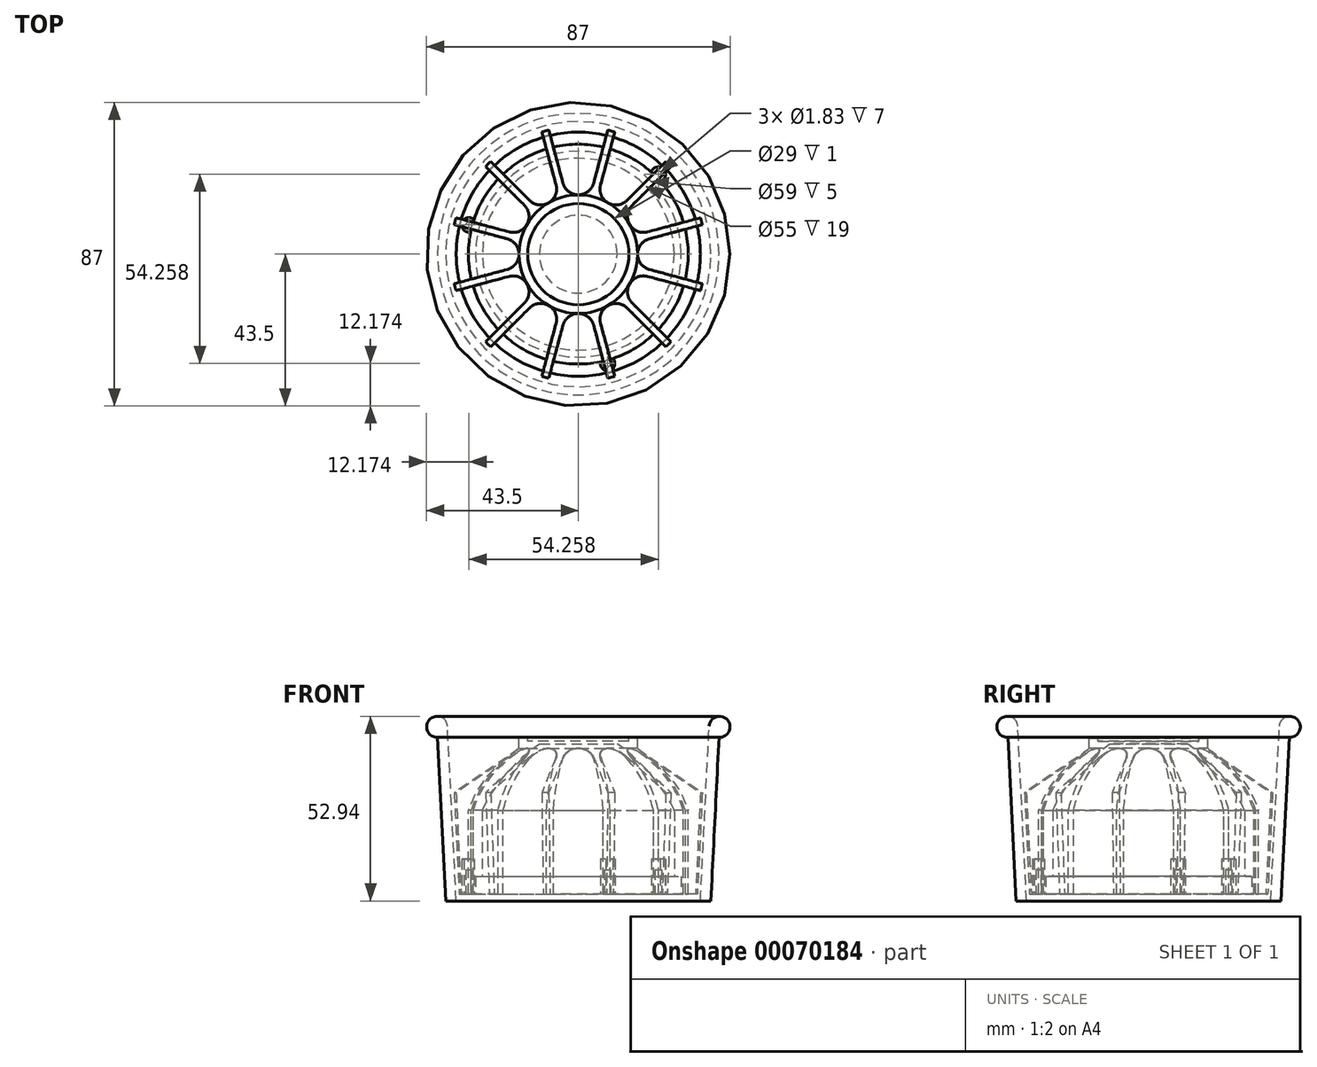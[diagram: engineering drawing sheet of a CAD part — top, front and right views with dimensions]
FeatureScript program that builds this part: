
annotation { "Feature Type Name" : "Feature", "Feature Type Description" : "" }
export const myFeature = defineFeature(function(context is Context, id is Id, definition is map)
    precondition{}
    {
        {
            var Q0;
            Q0=qCreatedBy(makeId("Right.planeOp"),FACE);
            var sketch = newSketch(context, id + "F0", { "sketchPlane" : qUnion([Q0])});
            skLineSegment(sketch, "E0.bottom", {"start": v(37.5, 50.09) * mm, "end": v(40.5, 49.94) * mm});
            skLineSegment(sketch, "E0.top", {"start": v(35, 0) * mm, "end": v(38, 0) * mm});
            skLineSegment(sketch, "E0.left", {"start": v(37.5, 50.09) * mm, "end": v(36.55, 31.11) * mm});
            skLineSegment(sketch, "E0.right", {"start": v(40.5, 49.94) * mm, "end": v(38, 0) * mm});
            skLineSegment(sketch, "E1", {"start": v(36.55, 31.11) * mm, "end": v(17, 43.74) * mm});
            skLineSegment(sketch, "E2", {"start": v(17, 43.74) * mm, "end": v(17, 46.74) * mm});
            skLineSegment(sketch, "E3", {"start": v(17, 46.74) * mm, "end": v(14.5, 46.74) * mm});
            skLineSegment(sketch, "E4", {"start": v(14.5, 46.74) * mm, "end": v(14.5, 45.74) * mm});
            skLineSegment(sketch, "E5", {"start": v(14.5, 45.74) * mm, "end": v(0, 45.74) * mm});
            skLineSegment(sketch, "E6", {"start": v(0, 45.74) * mm, "end": v(0, 0) * mm});
            skLineSegment(sketch, "E7", {"start": v(0, 0) * mm, "end": v(35, 0) * mm});
            skPoint(sketch, "E8.second.point", {"position": v(33.82, 50.09) * mm});
            skArc(sketch, "E9", {"start": v(40.35, 46.94) * mm, "mid": v(42.72, 51.95) * mm, "end": v(37.5, 50.09) * mm});
            skSolve(sketch);
        }
        {
            var Q0;
            {var subQ0=sQuery(id+"F0.wireOp",EDGE,"E0.top");Q0=makeQuery(id+"F0.imprint","IMPRINT",FACE,{"disambiguationData":[TD([[makeQuery(id+"F0.imprint","IMPRINT",EDGE,{"derivedFrom":subQ0}),1.0]])]});}
            var Q1;
            {var subQ0=sQuery(id+"F0.wireOp",EDGE,"E0.bottom");Q1=makeQuery(id+"F0.imprint","IMPRINT",FACE,{"disambiguationData":[TD([[makeQuery(id+"F0.imprint","IMPRINT",EDGE,{"derivedFrom":subQ0}),-1.0]])]});}
            var Q2;
            {var subQ0=sQuery(id+"F0.wireOp",EDGE,"E0.bottom");Q2=makeQuery(id+"F0.imprint","IMPRINT",FACE,{"disambiguationData":[TD([[makeQuery(id+"F0.imprint","IMPRINT",EDGE,{"derivedFrom":subQ0}),1.0]])]});}
            var Q3;
            Q3=sQuery(id+"F0.wireOp",EDGE,"E6");
            revolve(context, id + "F1", {"entities" : qUnion([Q0, Q1, Q2]), "axis" : qUnion([Q3]), "revolveType" : RevolveType.FULL});
        }
        {
            var Q0;
            Q0=makeQuery(id+"F1.opRevolve","SWEPT_FACE",FACE,{"disambiguationData":[OSD([sQuery(id+"F0.wireOp",EDGE,"E5")])]});
            var sketch = newSketch(context, id + "F2", { "sketchPlane" : qUnion([Q0])});
            skCircle(sketch, "E10.0", {"center": v(0, 0) * mm, "radius": 37.5 * mm, "construction": true});
            skCircle(sketch, "E11.0", {"center": v(0, 0) * mm, "radius": 17 * mm, "construction": true});
            skLineSegment(sketch, "E12", {"start": v(-8.71, 36.47) * mm, "end": v(-4.4, 20.37) * mm});
            skLineSegment(sketch, "E13", {"start": v(8.71, 36.47) * mm, "end": v(4.4, 20.37) * mm});
            skArc(sketch, "E14", {"start": v(-4.4, 20.37) * mm, "mid": v(-2.77, 17.94) * mm, "end": v(0, 17) * mm});
            skArc(sketch, "E15", {"start": v(0, 17) * mm, "mid": v(2.77, 17.94) * mm, "end": v(4.4, 20.37) * mm});
            skArc(sketch, "E16", {"start": v(8.71, 36.47) * mm, "mid": v(0, 37.5) * mm, "end": v(-8.71, 36.47) * mm});
            skLineSegment(sketch, "E17.1.0", {"start": v(25.78, 27.23) * mm, "end": v(14, 15.45) * mm});
            skArc(sketch, "E17.1.1", {"start": v(8.5, 14.72) * mm, "mid": v(11.37, 14.15) * mm, "end": v(14, 15.45) * mm});
            skArc(sketch, "E17.1.2", {"start": v(6.38, 19.84) * mm, "mid": v(6.57, 16.92) * mm, "end": v(8.5, 14.72) * mm});
            skLineSegment(sketch, "E17.1.3", {"start": v(10.7, 35.94) * mm, "end": v(6.38, 19.84) * mm});
            skArc(sketch, "E17.1.4", {"start": v(25.78, 27.23) * mm, "mid": v(18.75, 32.48) * mm, "end": v(10.7, 35.94) * mm});
            skLineSegment(sketch, "E17.2.0", {"start": v(35.94, 10.7) * mm, "end": v(19.84, 6.38) * mm});
            skArc(sketch, "E17.2.1", {"start": v(14.72, 8.5) * mm, "mid": v(16.92, 6.57) * mm, "end": v(19.84, 6.38) * mm});
            skArc(sketch, "E17.2.2", {"start": v(15.45, 14) * mm, "mid": v(14.15, 11.37) * mm, "end": v(14.72, 8.5) * mm});
            skLineSegment(sketch, "E17.2.3", {"start": v(27.23, 25.78) * mm, "end": v(15.45, 14) * mm});
            skArc(sketch, "E17.2.4", {"start": v(35.94, 10.7) * mm, "mid": v(32.48, 18.75) * mm, "end": v(27.23, 25.78) * mm});
            skLineSegment(sketch, "E17.3.0", {"start": v(36.47, -8.71) * mm, "end": v(20.37, -4.4) * mm});
            skArc(sketch, "E17.3.1", {"start": v(17, 0) * mm, "mid": v(17.94, -2.77) * mm, "end": v(20.37, -4.4) * mm});
            skArc(sketch, "E17.3.2", {"start": v(20.37, 4.4) * mm, "mid": v(17.94, 2.77) * mm, "end": v(17, 0) * mm});
            skLineSegment(sketch, "E17.3.3", {"start": v(36.47, 8.71) * mm, "end": v(20.37, 4.4) * mm});
            skArc(sketch, "E17.3.4", {"start": v(36.47, -8.71) * mm, "mid": v(37.5, 0) * mm, "end": v(36.47, 8.71) * mm});
            skLineSegment(sketch, "E17.4.0", {"start": v(27.23, -25.78) * mm, "end": v(15.45, -14) * mm});
            skArc(sketch, "E17.4.1", {"start": v(14.72, -8.5) * mm, "mid": v(14.15, -11.37) * mm, "end": v(15.45, -14) * mm});
            skArc(sketch, "E17.4.2", {"start": v(19.84, -6.38) * mm, "mid": v(16.92, -6.57) * mm, "end": v(14.72, -8.5) * mm});
            skLineSegment(sketch, "E17.4.3", {"start": v(35.94, -10.7) * mm, "end": v(19.84, -6.38) * mm});
            skArc(sketch, "E17.4.4", {"start": v(27.23, -25.78) * mm, "mid": v(32.48, -18.75) * mm, "end": v(35.94, -10.7) * mm});
            skLineSegment(sketch, "E17.5.0", {"start": v(10.7, -35.94) * mm, "end": v(6.38, -19.84) * mm});
            skArc(sketch, "E17.5.1", {"start": v(8.5, -14.72) * mm, "mid": v(6.57, -16.92) * mm, "end": v(6.38, -19.84) * mm});
            skArc(sketch, "E17.5.2", {"start": v(14, -15.45) * mm, "mid": v(11.37, -14.15) * mm, "end": v(8.5, -14.72) * mm});
            skLineSegment(sketch, "E17.5.3", {"start": v(25.78, -27.23) * mm, "end": v(14, -15.45) * mm});
            skArc(sketch, "E17.5.4", {"start": v(10.7, -35.94) * mm, "mid": v(18.75, -32.48) * mm, "end": v(25.78, -27.23) * mm});
            skLineSegment(sketch, "E17.6.0", {"start": v(-8.71, -36.47) * mm, "end": v(-4.4, -20.37) * mm});
            skArc(sketch, "E17.6.1", {"start": v(0, -17) * mm, "mid": v(-2.77, -17.94) * mm, "end": v(-4.4, -20.37) * mm});
            skArc(sketch, "E17.6.2", {"start": v(4.4, -20.37) * mm, "mid": v(2.77, -17.94) * mm, "end": v(0, -17) * mm});
            skLineSegment(sketch, "E17.6.3", {"start": v(8.71, -36.47) * mm, "end": v(4.4, -20.37) * mm});
            skArc(sketch, "E17.6.4", {"start": v(-8.71, -36.47) * mm, "mid": v(0, -37.5) * mm, "end": v(8.71, -36.47) * mm});
            skLineSegment(sketch, "E17.7.0", {"start": v(-25.78, -27.23) * mm, "end": v(-14, -15.45) * mm});
            skArc(sketch, "E17.7.1", {"start": v(-8.5, -14.72) * mm, "mid": v(-11.37, -14.15) * mm, "end": v(-14, -15.45) * mm});
            skArc(sketch, "E17.7.2", {"start": v(-6.38, -19.84) * mm, "mid": v(-6.57, -16.92) * mm, "end": v(-8.5, -14.72) * mm});
            skLineSegment(sketch, "E17.7.3", {"start": v(-10.7, -35.94) * mm, "end": v(-6.38, -19.84) * mm});
            skArc(sketch, "E17.7.4", {"start": v(-25.78, -27.23) * mm, "mid": v(-18.75, -32.48) * mm, "end": v(-10.7, -35.94) * mm});
            skLineSegment(sketch, "E17.8.0", {"start": v(-35.94, -10.7) * mm, "end": v(-19.84, -6.38) * mm});
            skArc(sketch, "E17.8.1", {"start": v(-14.72, -8.5) * mm, "mid": v(-16.92, -6.57) * mm, "end": v(-19.84, -6.38) * mm});
            skArc(sketch, "E17.8.2", {"start": v(-15.45, -14) * mm, "mid": v(-14.15, -11.37) * mm, "end": v(-14.72, -8.5) * mm});
            skLineSegment(sketch, "E17.8.3", {"start": v(-27.23, -25.78) * mm, "end": v(-15.45, -14) * mm});
            skArc(sketch, "E17.8.4", {"start": v(-35.94, -10.7) * mm, "mid": v(-32.48, -18.75) * mm, "end": v(-27.23, -25.78) * mm});
            skLineSegment(sketch, "E17.9.0", {"start": v(-36.47, 8.71) * mm, "end": v(-20.37, 4.4) * mm});
            skArc(sketch, "E17.9.1", {"start": v(-17, 0) * mm, "mid": v(-17.94, 2.77) * mm, "end": v(-20.37, 4.4) * mm});
            skArc(sketch, "E17.9.2", {"start": v(-20.37, -4.4) * mm, "mid": v(-17.94, -2.77) * mm, "end": v(-17, 0) * mm});
            skLineSegment(sketch, "E17.9.3", {"start": v(-36.47, -8.71) * mm, "end": v(-20.37, -4.4) * mm});
            skArc(sketch, "E17.9.4", {"start": v(-36.47, 8.71) * mm, "mid": v(-37.5, 0) * mm, "end": v(-36.47, -8.71) * mm});
            skLineSegment(sketch, "E17.10.0", {"start": v(-27.23, 25.78) * mm, "end": v(-15.45, 14) * mm});
            skArc(sketch, "E17.10.1", {"start": v(-14.72, 8.5) * mm, "mid": v(-14.15, 11.37) * mm, "end": v(-15.45, 14) * mm});
            skArc(sketch, "E17.10.2", {"start": v(-19.84, 6.38) * mm, "mid": v(-16.92, 6.57) * mm, "end": v(-14.72, 8.5) * mm});
            skLineSegment(sketch, "E17.10.3", {"start": v(-35.94, 10.7) * mm, "end": v(-19.84, 6.38) * mm});
            skArc(sketch, "E17.10.4", {"start": v(-27.23, 25.78) * mm, "mid": v(-32.48, 18.75) * mm, "end": v(-35.94, 10.7) * mm});
            skLineSegment(sketch, "E17.11.0", {"start": v(-10.7, 35.94) * mm, "end": v(-6.38, 19.84) * mm});
            skArc(sketch, "E17.11.1", {"start": v(-8.5, 14.72) * mm, "mid": v(-6.57, 16.92) * mm, "end": v(-6.38, 19.84) * mm});
            skArc(sketch, "E17.11.2", {"start": v(-14, 15.45) * mm, "mid": v(-11.37, 14.15) * mm, "end": v(-8.5, 14.72) * mm});
            skLineSegment(sketch, "E17.11.3", {"start": v(-25.78, 27.23) * mm, "end": v(-14, 15.45) * mm});
            skArc(sketch, "E17.11.4", {"start": v(-10.7, 35.94) * mm, "mid": v(-18.75, 32.48) * mm, "end": v(-25.78, 27.23) * mm});
            skLineSegment(sketch, "E17.anchor1", {"start": v(0, 0) * mm, "end": v(4.4, 20.37) * mm, "construction": true});
            skLineSegment(sketch, "E17.anchor2", {"start": v(0, 0) * mm, "end": v(-6.38, 19.84) * mm, "construction": true});
            skLineSegment(sketch, "E18", {"start": v(8.71, 36.47) * mm, "end": v(10.7, 35.94) * mm, "construction": true});
            skLineSegment(sketch, "E19", {"start": v(4.4, 20.37) * mm, "end": v(6.38, 19.84) * mm, "construction": true});
            skSolve(sketch);
        }
        {
            var Q0;
            Q0=makeQuery(id+"F2.imprint","IMPRINT",FACE,{"disambiguationData":[TD([[makeQuery(id+"F2.imprint","IMPRINT",EDGE,{"derivedFrom":sQuery(id+"F2.wireOp",EDGE,"E12")}),1.0]])]});
            var Q1;
            Q1=makeQuery(id+"F2.imprint","IMPRINT",FACE,{"disambiguationData":[TD([[makeQuery(id+"F2.imprint","IMPRINT",EDGE,{"derivedFrom":sQuery(id+"F2.wireOp",EDGE,"E17.1.0")}),-1.0]])]});
            var Q2;
            Q2=makeQuery(id+"F2.imprint","IMPRINT",FACE,{"disambiguationData":[TD([[makeQuery(id+"F2.imprint","IMPRINT",EDGE,{"derivedFrom":sQuery(id+"F2.wireOp",EDGE,"E17.2.0")}),-1.0]])]});
            var Q3;
            Q3=makeQuery(id+"F2.imprint","IMPRINT",FACE,{"disambiguationData":[TD([[makeQuery(id+"F2.imprint","IMPRINT",EDGE,{"derivedFrom":sQuery(id+"F2.wireOp",EDGE,"E17.3.0")}),-1.0]])]});
            var Q4;
            Q4=makeQuery(id+"F2.imprint","IMPRINT",FACE,{"disambiguationData":[TD([[makeQuery(id+"F2.imprint","IMPRINT",EDGE,{"derivedFrom":sQuery(id+"F2.wireOp",EDGE,"E17.4.0")}),-1.0]])]});
            var Q5;
            Q5=makeQuery(id+"F2.imprint","IMPRINT",FACE,{"disambiguationData":[TD([[makeQuery(id+"F2.imprint","IMPRINT",EDGE,{"derivedFrom":sQuery(id+"F2.wireOp",EDGE,"E17.5.0")}),-1.0]])]});
            var Q6;
            Q6=makeQuery(id+"F2.imprint","IMPRINT",FACE,{"disambiguationData":[TD([[makeQuery(id+"F2.imprint","IMPRINT",EDGE,{"derivedFrom":sQuery(id+"F2.wireOp",EDGE,"E17.6.0")}),-1.0]])]});
            var Q7;
            Q7=makeQuery(id+"F2.imprint","IMPRINT",FACE,{"disambiguationData":[TD([[makeQuery(id+"F2.imprint","IMPRINT",EDGE,{"derivedFrom":sQuery(id+"F2.wireOp",EDGE,"E17.7.0")}),-1.0]])]});
            var Q8;
            Q8=makeQuery(id+"F2.imprint","IMPRINT",FACE,{"disambiguationData":[TD([[makeQuery(id+"F2.imprint","IMPRINT",EDGE,{"derivedFrom":sQuery(id+"F2.wireOp",EDGE,"E17.8.0")}),-1.0]])]});
            var Q9;
            Q9=makeQuery(id+"F2.imprint","IMPRINT",FACE,{"disambiguationData":[TD([[makeQuery(id+"F2.imprint","IMPRINT",EDGE,{"derivedFrom":sQuery(id+"F2.wireOp",EDGE,"E17.9.0")}),-1.0]])]});
            var Q10;
            Q10=makeQuery(id+"F2.imprint","IMPRINT",FACE,{"disambiguationData":[TD([[makeQuery(id+"F2.imprint","IMPRINT",EDGE,{"derivedFrom":sQuery(id+"F2.wireOp",EDGE,"E17.10.0")}),-1.0]])]});
            var Q11;
            Q11=makeQuery(id+"F2.imprint","IMPRINT",FACE,{"disambiguationData":[TD([[makeQuery(id+"F2.imprint","IMPRINT",EDGE,{"derivedFrom":sQuery(id+"F2.wireOp",EDGE,"E17.11.0")}),-1.0]])]});
            extrude(context, id + "F3", {"entities" : qUnion([Q0, Q1, Q2, Q3, Q4, Q5, Q6, Q7, Q8, Q9, Q10, Q11]), "operationType" : NewBodyOperationType.REMOVE, "endBound" : BoundingType.THROUGH_ALL, "oppositeDirection" : true, "depth" : 25 * mm});
        }
        {
            var Q0;
            Q0=qCreatedBy(makeId("Right.planeOp"),FACE);
            var sketch = newSketch(context, id + "F4", { "sketchPlane" : qUnion([Q0])});
            skLineSegment(sketch, "E20.0.0", {"start": v(40.5, 49.94) * mm, "end": v(37.5, 50.09) * mm, "construction": true});
            skLineSegment(sketch, "E20.0.1", {"start": v(37.5, 50.09) * mm, "end": v(36.55, 31.11) * mm, "construction": true});
            skLineSegment(sketch, "E20.0.2", {"start": v(36.55, 31.11) * mm, "end": v(17, 43.74) * mm, "construction": true});
            skLineSegment(sketch, "E20.0.3", {"start": v(17, 43.74) * mm, "end": v(17, 46.74) * mm, "construction": true});
            skLineSegment(sketch, "E20.0.4", {"start": v(17, 46.74) * mm, "end": v(14.5, 46.74) * mm, "construction": true});
            skLineSegment(sketch, "E20.0.5", {"start": v(14.5, 46.74) * mm, "end": v(14.5, 45.74) * mm, "construction": true});
            skLineSegment(sketch, "E20.0.6", {"start": v(14.5, 45.74) * mm, "end": v(0, 45.74) * mm, "construction": true});
            skLineSegment(sketch, "E20.0.7", {"start": v(0, 45.74) * mm, "end": v(0, 0) * mm, "construction": true});
            skLineSegment(sketch, "E20.0.8", {"start": v(0, 0) * mm, "end": v(35, 0) * mm, "construction": true});
            skLineSegment(sketch, "E20.0.9", {"start": v(35, 0) * mm, "end": v(38, 0) * mm, "construction": true});
            skLineSegment(sketch, "E20.0.10", {"start": v(38, 0) * mm, "end": v(40.35, 46.94) * mm, "construction": true});
            skLineSegment(sketch, "E20.0.11", {"start": v(40.35, 46.94) * mm, "end": v(40.5, 49.94) * mm, "construction": true});
            skLineSegment(sketch, "E21", {"start": v(27.5, 7) * mm, "end": v(27.5, 26) * mm});
            skFitSpline(sketch, "E22", {"points": [v(27.5, 26) * mm, v(11.15, 45) * mm], "startDerivative": vector(-8.78, 19.56) * mm, "endDerivative": vector(-20.78, 14.04) * mm});
            skLineSegment(sketch, "E23", {"start": v(11.15, 45) * mm, "end": v(0, 45) * mm});
            skLineSegment(sketch, "E24", {"start": v(0, 45) * mm, "end": v(0, 0) * mm});
            skLineSegment(sketch, "E25", {"start": v(0, 0) * mm, "end": v(36.5, 0) * mm});
            skLineSegment(sketch, "E26", {"start": v(29.5, 2) * mm, "end": v(29.5, 7) * mm});
            skLineSegment(sketch, "E27", {"start": v(27.5, 7) * mm, "end": v(29.5, 7) * mm});
            skLineSegment(sketch, "E28", {"start": v(29.5, 2) * mm, "end": v(31.5, 2) * mm});
            skLineSegment(sketch, "E29", {"start": v(31.5, 2) * mm, "end": v(31.5, 26) * mm});
            skFitSpline(sketch, "E30", {"points": [v(31.5, 26) * mm, v(17, 43.74) * mm], "startDerivative": vector(-9.93, 28.81) * mm, "endDerivative": vector(-15.85, 12) * mm});
            skLineSegment(sketch, "E31", {"start": v(17, 43.74) * mm, "end": v(14.5, 45.74) * mm});
            skLineSegment(sketch, "E32", {"start": v(14.5, 45.74) * mm, "end": v(0, 45.74) * mm});
            skLineSegment(sketch, "E33", {"start": v(0, 45.74) * mm, "end": v(0, 45) * mm});
            skLineSegment(sketch, "E34.bottom", {"start": v(37.5, 50.09) * mm, "end": v(40.5, 49.94) * mm});
            skLineSegment(sketch, "E34.top", {"start": v(35, 0) * mm, "end": v(38, 0) * mm});
            skLineSegment(sketch, "E34.left", {"start": v(37.5, 50.09) * mm, "end": v(35, 0) * mm});
            skLineSegment(sketch, "E34.right", {"start": v(40.5, 49.94) * mm, "end": v(38, 0) * mm});
            skLineSegment(sketch, "E35", {"start": v(36.5, 0) * mm, "end": v(36.5, 2) * mm});
            skLineSegment(sketch, "E36", {"start": v(31.5, 2) * mm, "end": v(36.5, 2) * mm});
            skSolve(sketch);
        }
        {
            var Q0;
            Q0=makeQuery(id+"F4.imprint","IMPRINT",FACE,{"disambiguationData":[TD([[makeQuery(id+"F4.imprint","IMPRINT",EDGE,{"derivedFrom":sQuery(id+"F4.wireOp",EDGE,"E21")}),1.0]])]});
            var Q1;
            Q1=sQuery(id+"F4.wireOp",EDGE,"E24");
            revolve(context, id + "F5", {"operationType" : NewBodyOperationType.REMOVE, "entities" : qUnion([Q0]), "axis" : qUnion([Q1]), "revolveType" : RevolveType.FULL, "oppositeDirection" : true});
        }
        {
            var Q0;
            Q0=makeQuery(id+"F4.imprint","IMPRINT",FACE,{"disambiguationData":[TD([[makeQuery(id+"F4.imprint","IMPRINT",EDGE,{"derivedFrom":sQuery(id+"F4.wireOp",EDGE,"E21")}),-1.0]])]});
            var Q1;
            Q1=makeQuery(id+"F4.imprint","IMPRINT",FACE,{"disambiguationData":[TD([[makeQuery(id+"F4.imprint","IMPRINT",EDGE,{"derivedFrom":sQuery(id+"F4.wireOp",EDGE,"E34.bottom")}),-1.0]])]});
            var Q2;
            {var subQ3=sQuery(id+"F4.wireOp",EDGE,"E35");Q2=makeQuery(id+"F4.imprint","IMPRINT",FACE,{"disambiguationData":[TD([[makeQuery(id+"F4.imprint","IMPRINT",EDGE,{"derivedFrom":subQ3}),1.0]])]});}
            var Q3;
            Q3=sQuery(id+"F4.wireOp",EDGE,"E24");
            revolve(context, id + "F6", {"operationType" : NewBodyOperationType.ADD, "entities" : qUnion([Q0, Q1, Q2]), "axis" : qUnion([Q3]), "revolveType" : RevolveType.FULL});
        }
        {
            var Q0;
            {var subQ0=sQuery(id+"F4.wireOp",EDGE,"E28");var subQ1=makeQuery(id+"F5.opRevolve","SWEPT_FACE",FACE,{"disambiguationData":[OSD([subQ0,sQuery(id+"F4.wireOp",EDGE,"E36")])]});Q0=makeQuery(id+"F6.boolean.opBoolean","MERGE",FACE,{"derivedFrom":[makeQuery(id+"F5.boolean.opBoolean","COPY",FACE,{"disambiguationData":[OD(0.0)],"derivedFrom":subQ1}),makeQuery(id+"F5.boolean.opBoolean","COPY",FACE,{"disambiguationData":[OD(1.0)],"derivedFrom":subQ1}),makeQuery(id+"F5.boolean.opBoolean","COPY",FACE,{"disambiguationData":[OD(2.0)],"derivedFrom":subQ1}),makeQuery(id+"F5.boolean.opBoolean","COPY",FACE,{"disambiguationData":[OD(3.0)],"derivedFrom":subQ1}),makeQuery(id+"F5.boolean.opBoolean","COPY",FACE,{"disambiguationData":[OD(4.0)],"derivedFrom":subQ1}),makeQuery(id+"F5.boolean.opBoolean","COPY",FACE,{"disambiguationData":[OD(5.0)],"derivedFrom":subQ1}),makeQuery(id+"F5.boolean.opBoolean","COPY",FACE,{"disambiguationData":[OD(6.0)],"derivedFrom":subQ1}),makeQuery(id+"F5.boolean.opBoolean","COPY",FACE,{"disambiguationData":[OD(7.0)],"derivedFrom":subQ1}),makeQuery(id+"F5.boolean.opBoolean","COPY",FACE,{"disambiguationData":[OD(8.0)],"derivedFrom":subQ1}),makeQuery(id+"F5.boolean.opBoolean","COPY",FACE,{"disambiguationData":[OD(9.0)],"derivedFrom":subQ1}),makeQuery(id+"F5.boolean.opBoolean","COPY",FACE,{"disambiguationData":[OD(10.0)],"derivedFrom":subQ1}),makeQuery(id+"F5.boolean.opBoolean","COPY",FACE,{"disambiguationData":[OD(11.0)],"derivedFrom":subQ1}),makeQuery(id+"F6.opRevolve","SWEPT_FACE",FACE,{"disambiguationData":[OSD([subQ0])]})]});}
            var sketch = newSketch(context, id + "F7", { "sketchPlane" : qUnion([Q0])});
            skCircle(sketch, "E37", {"center": v(8.4, 31.33) * mm, "radius": 2.09 * mm});
            skLineSegment(sketch, "E38", {"start": v(0, 0) * mm, "end": v(9.08, 33.9) * mm, "construction": true});
            skCircle(sketch, "E39", {"center": v(8.4, 31.33) * mm, "radius": 0.92 * mm});
            skCircle(sketch, "E40.1.0", {"center": v(-31.33, -8.4) * mm, "radius": 0.92 * mm});
            skCircle(sketch, "E40.1.1", {"center": v(-31.33, -8.4) * mm, "radius": 2.09 * mm});
            skCircle(sketch, "E40.2.0", {"center": v(22.93, -22.93) * mm, "radius": 0.92 * mm});
            skCircle(sketch, "E40.2.1", {"center": v(22.93, -22.93) * mm, "radius": 2.09 * mm});
            skPoint(sketch, "E40.center", {"position": v(0, 0) * mm});
            skSolve(sketch);
        }
        {
            var Q0;
            {var subQ0=sQuery(id+"F7.wireOp",EDGE,"E37");var subQ1=sQuery(id+"F4.wireOp",EDGE,"E36");var subQ2=sQuery(id+"F4.wireOp",EDGE,"E28");var subQ3=makeQuery(id+"F5.opRevolve","SWEPT_FACE",FACE,{"disambiguationData":[OSD([subQ2,subQ1])]});var subQ4=makeQuery(id+"F3.boolean.opBoolean","COPY",FACE,{"derivedFrom":makeQuery(id+"F3.opExtrude","SWEPT_FACE",FACE,{"disambiguationData":[OSD([sQuery(id+"F2.wireOp",EDGE,"E17.6.3")])]})});var subQ5=makeQuery(id+"F5.boolean.opBoolean","INTERSECT",EDGE,{"derivedFrom":[subQ4,subQ3]});var subQ6=makeQuery(id+"F7.imprint","INTERSECT",VERTEX,{"derivedFrom":[subQ5,subQ0]});Q0=makeQuery(id+"F7.imprint","IMPRINT",FACE,{"disambiguationData":[TD([[makeQuery(id+"F7.imprint","IMPRINT",EDGE,{"disambiguationData":[TD([[subQ6,-1.0]])],"derivedFrom":subQ0}),1.0]])]});}
            var Q1;
            {var subQ0=sQuery(id+"F7.wireOp",EDGE,"E37");var subQ1=sQuery(id+"F4.wireOp",EDGE,"E36");var subQ2=sQuery(id+"F4.wireOp",EDGE,"E28");var subQ3=makeQuery(id+"F5.opRevolve","SWEPT_FACE",FACE,{"disambiguationData":[OSD([subQ2,subQ1])]});var subQ4=makeQuery(id+"F3.boolean.opBoolean","COPY",FACE,{"derivedFrom":makeQuery(id+"F3.opExtrude","SWEPT_FACE",FACE,{"disambiguationData":[OSD([sQuery(id+"F2.wireOp",EDGE,"E17.5.0")])]})});var subQ5=makeQuery(id+"F5.boolean.opBoolean","INTERSECT",EDGE,{"derivedFrom":[subQ4,subQ3]});var subQ6=makeQuery(id+"F7.imprint","INTERSECT",VERTEX,{"derivedFrom":[subQ5,subQ0]});Q1=makeQuery(id+"F7.imprint","IMPRINT",FACE,{"disambiguationData":[TD([[makeQuery(id+"F7.imprint","IMPRINT",EDGE,{"disambiguationData":[TD([[subQ6,1.0]])],"derivedFrom":subQ0}),1.0]])]});}
            var Q2;
            {var subQ0=sQuery(id+"F7.wireOp",EDGE,"E40.2.1");var subQ1=sQuery(id+"F4.wireOp",EDGE,"E36");var subQ2=sQuery(id+"F4.wireOp",EDGE,"E28");var subQ3=makeQuery(id+"F5.opRevolve","SWEPT_FACE",FACE,{"disambiguationData":[OSD([subQ2,subQ1])]});var subQ4=makeQuery(id+"F3.boolean.opBoolean","COPY",FACE,{"derivedFrom":makeQuery(id+"F3.opExtrude","SWEPT_FACE",FACE,{"disambiguationData":[OSD([sQuery(id+"F2.wireOp",EDGE,"E17.2.3")])]})});var subQ5=makeQuery(id+"F5.boolean.opBoolean","INTERSECT",EDGE,{"derivedFrom":[subQ4,subQ3]});var subQ6=makeQuery(id+"F7.imprint","INTERSECT",VERTEX,{"derivedFrom":[subQ5,subQ0]});Q2=makeQuery(id+"F7.imprint","IMPRINT",FACE,{"disambiguationData":[TD([[makeQuery(id+"F7.imprint","IMPRINT",EDGE,{"disambiguationData":[TD([[subQ6,-1.0]])],"derivedFrom":subQ0}),1.0]])]});}
            var Q3;
            {var subQ0=sQuery(id+"F7.wireOp",EDGE,"E40.2.1");var subQ1=sQuery(id+"F4.wireOp",EDGE,"E36");var subQ2=sQuery(id+"F4.wireOp",EDGE,"E28");var subQ3=makeQuery(id+"F5.opRevolve","SWEPT_FACE",FACE,{"disambiguationData":[OSD([subQ2,subQ1])]});var subQ4=makeQuery(id+"F3.boolean.opBoolean","COPY",FACE,{"derivedFrom":makeQuery(id+"F3.opExtrude","SWEPT_FACE",FACE,{"disambiguationData":[OSD([sQuery(id+"F2.wireOp",EDGE,"E17.1.0")])]})});var subQ5=makeQuery(id+"F5.boolean.opBoolean","INTERSECT",EDGE,{"derivedFrom":[subQ4,subQ3]});var subQ6=makeQuery(id+"F7.imprint","INTERSECT",VERTEX,{"derivedFrom":[subQ5,subQ0]});Q3=makeQuery(id+"F7.imprint","IMPRINT",FACE,{"disambiguationData":[TD([[makeQuery(id+"F7.imprint","IMPRINT",EDGE,{"disambiguationData":[TD([[subQ6,1.0]])],"derivedFrom":subQ0}),1.0]])]});}
            var Q4;
            {var subQ0=sQuery(id+"F7.wireOp",EDGE,"E40.1.1");var subQ1=sQuery(id+"F4.wireOp",EDGE,"E36");var subQ2=sQuery(id+"F4.wireOp",EDGE,"E28");var subQ3=makeQuery(id+"F5.opRevolve","SWEPT_FACE",FACE,{"disambiguationData":[OSD([subQ2,subQ1])]});var subQ4=makeQuery(id+"F3.boolean.opBoolean","COPY",FACE,{"derivedFrom":makeQuery(id+"F3.opExtrude","SWEPT_FACE",FACE,{"disambiguationData":[OSD([sQuery(id+"F2.wireOp",EDGE,"E17.10.3")])]})});var subQ5=makeQuery(id+"F5.boolean.opBoolean","INTERSECT",EDGE,{"derivedFrom":[subQ4,subQ3]});var subQ6=makeQuery(id+"F7.imprint","INTERSECT",VERTEX,{"derivedFrom":[subQ5,subQ0]});Q4=makeQuery(id+"F7.imprint","IMPRINT",FACE,{"disambiguationData":[TD([[makeQuery(id+"F7.imprint","IMPRINT",EDGE,{"disambiguationData":[TD([[subQ6,-1.0]])],"derivedFrom":subQ0}),1.0]])]});}
            var Q5;
            {var subQ0=sQuery(id+"F7.wireOp",EDGE,"E40.1.1");var subQ1=sQuery(id+"F4.wireOp",EDGE,"E36");var subQ2=sQuery(id+"F4.wireOp",EDGE,"E28");var subQ3=makeQuery(id+"F5.opRevolve","SWEPT_FACE",FACE,{"disambiguationData":[OSD([subQ2,subQ1])]});var subQ4=makeQuery(id+"F3.boolean.opBoolean","COPY",FACE,{"derivedFrom":makeQuery(id+"F3.opExtrude","SWEPT_FACE",FACE,{"disambiguationData":[OSD([sQuery(id+"F2.wireOp",EDGE,"E17.9.0")])]})});var subQ5=makeQuery(id+"F5.boolean.opBoolean","INTERSECT",EDGE,{"derivedFrom":[subQ4,subQ3]});var subQ6=makeQuery(id+"F7.imprint","INTERSECT",VERTEX,{"derivedFrom":[subQ5,subQ0]});Q5=makeQuery(id+"F7.imprint","IMPRINT",FACE,{"disambiguationData":[TD([[makeQuery(id+"F7.imprint","IMPRINT",EDGE,{"disambiguationData":[TD([[subQ6,1.0]])],"derivedFrom":subQ0}),1.0]])]});}
            extrude(context, id + "F8", {"entities" : qUnion([Q0, Q1, Q2, Q3, Q4, Q5]), "operationType" : NewBodyOperationType.ADD, "oppositeDirection" : true, "depth" : 10 * mm});
        }
        {
            var Q0;
            Q0=makeQuery(id+"F7.imprint","IMPRINT",FACE,{"disambiguationData":[TD([[makeQuery(id+"F7.imprint","IMPRINT",EDGE,{"derivedFrom":sQuery(id+"F7.wireOp",EDGE,"E39")}),1.0]])]});
            var Q1;
            Q1=makeQuery(id+"F7.imprint","IMPRINT",FACE,{"disambiguationData":[TD([[makeQuery(id+"F7.imprint","IMPRINT",EDGE,{"derivedFrom":sQuery(id+"F7.wireOp",EDGE,"E40.2.0")}),1.0]])]});
            var Q2;
            Q2=makeQuery(id+"F7.imprint","IMPRINT",FACE,{"disambiguationData":[TD([[makeQuery(id+"F7.imprint","IMPRINT",EDGE,{"derivedFrom":sQuery(id+"F7.wireOp",EDGE,"E40.1.0")}),1.0]])]});
            extrude(context, id + "F9", {"entities" : qUnion([Q0, Q1, Q2]), "operationType" : NewBodyOperationType.REMOVE, "oppositeDirection" : true, "depth" : 7 * mm});
        }
    });
